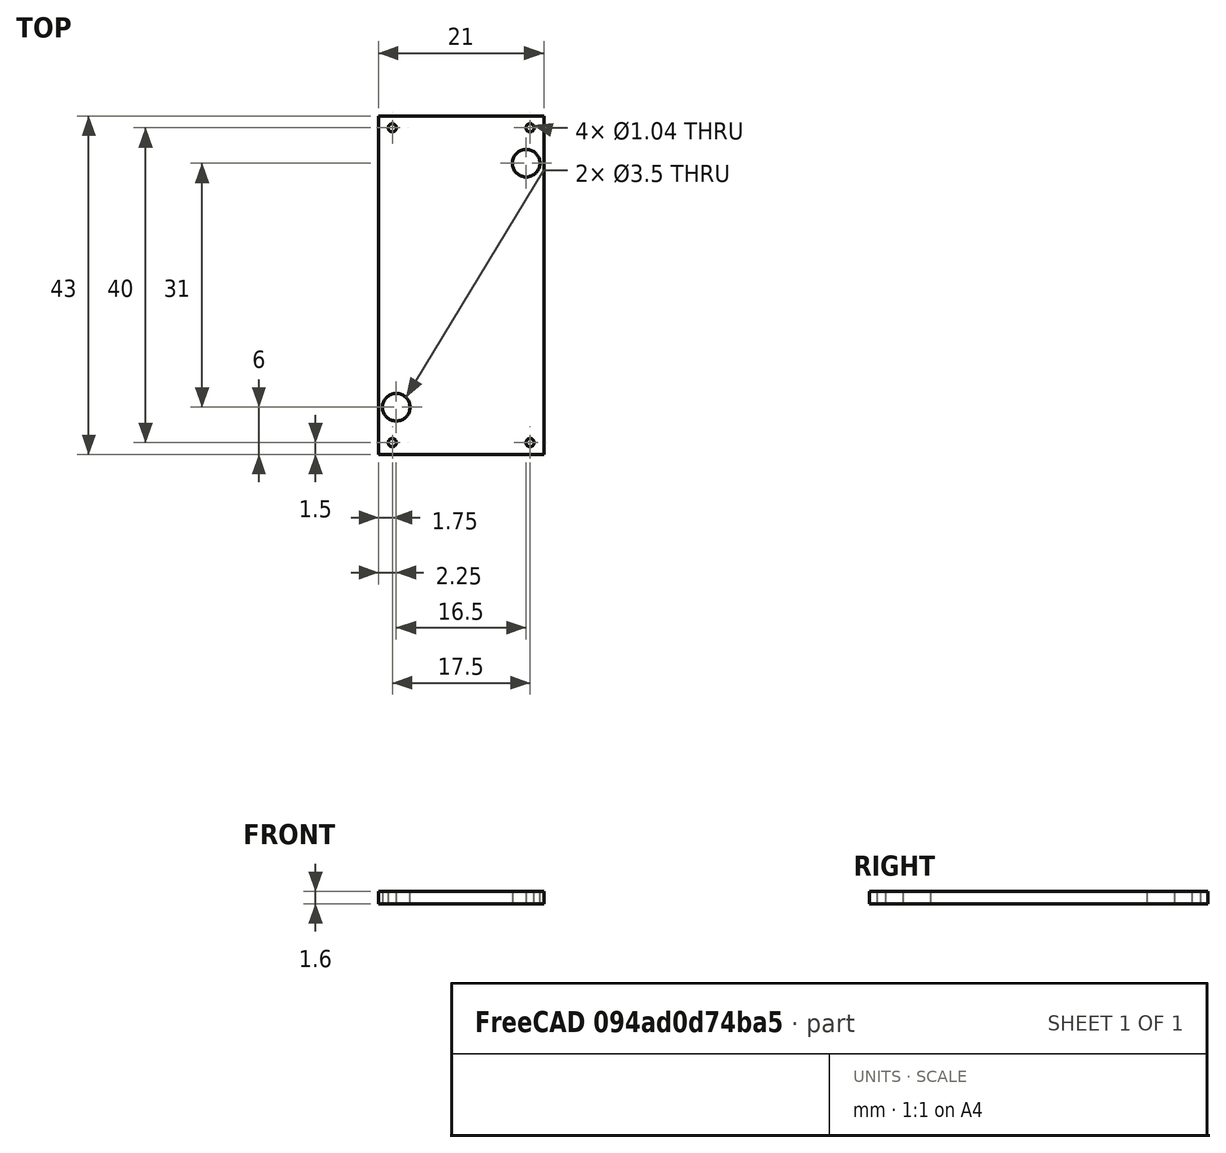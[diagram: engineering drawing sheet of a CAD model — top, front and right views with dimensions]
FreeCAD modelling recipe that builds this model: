
FCSTD DOCUMENT  (FreeCAD 0.20R27422 (Git))
Label: LM2596_Board
License: All rights reserved
LicenseURL: http://en.wikipedia.org/wiki/All_rights_reserved
objects: Sketcher::SketchObject×2, PartDesign::Pad×1, PartDesign::Body×1
note: 5 computed .brp shape members not serialized (recipe doc carries the construction recipe); baked Part::Feature solids carry a one-line shape summary decoded from their .brp

FEATURE [Sketcher::SketchObject] Sketch
  FullyConstrained = true
  MapMode = 5
  Support = -> [XY_Plane]
  sketch-geometry (11):
    g0: LineSegment StartX=-10.5 StartY=21.5 StartZ=0 EndX=10.5 EndY=21.5 EndZ=0
    g1: LineSegment StartX=10.5 StartY=21.5 StartZ=0 EndX=10.5 EndY=-21.5 EndZ=0
    g2: LineSegment StartX=10.5 StartY=-21.5 StartZ=0 EndX=-10.5 EndY=-21.5 EndZ=0
    g3: LineSegment StartX=-10.5 StartY=-21.5 StartZ=0 EndX=-10.5 EndY=21.5 EndZ=0
    g4: Circle CenterX=-8.75 CenterY=20 CenterZ=0 NormalX=0 NormalY=0 NormalZ=1 AngleXU=0 Radius=0.52
    g5: Circle CenterX=8.75 CenterY=20 CenterZ=0 NormalX=0 NormalY=0 NormalZ=1 AngleXU=0 Radius=0.52
    g6: LineSegment StartX=-8.75 StartY=20 StartZ=0 EndX=8.75 EndY=20 EndZ=0
    g7: Circle CenterX=-8.75 CenterY=-20 CenterZ=0 NormalX=0 NormalY=0 NormalZ=1 AngleXU=0 Radius=0.52
    g8: Circle CenterX=8.75 CenterY=-20 CenterZ=0 NormalX=0 NormalY=0 NormalZ=1 AngleXU=0 Radius=0.52
    g9: Circle CenterX=-8.25 CenterY=-15.5 CenterZ=0 NormalX=0 NormalY=0 NormalZ=1 AngleXU=0 Radius=1.75
    g10: Circle CenterX=8.25 CenterY=15.5 CenterZ=0 NormalX=0 NormalY=0 NormalZ=1 AngleXU=0 Radius=1.75
  constraints (27):
    c: Coincident(g0,g1)
    c: Coincident(g1,g2)
    c: Coincident(g2,g3)
    c: Coincident(g3,g0)
    c: Horizontal(g0)
    c: Horizontal(g2)
    c: Vertical(g1)
    c: Vertical(g3)
    c: Symmetric(g0,g1,g-1)
    c: DistanceX(g0,g0) = 21
    c: DistanceY(g3,g3) = 43
    c: Coincident(g6,g4)
    c: Coincident(g6,g5)
    c: DistanceX(g6,g6) = 17.5
    c: Symmetric(g5,g4,g-2)
    c: Symmetric(g5,g7,g-1)
    c: Symmetric(g8,g4,g-1)
    c: DistanceY(g7,g4) = 40
    c: Equal(g8,g7)
    c: Equal(g7,g5)
    c: Equal(g5,g4)
    c: Diameter(g8) = 1.04
    c: Diameter(g9) = 3.5
    c: DistanceY(g8,g9) = 4.5
    c: Equal(g10,g9)
    c: Symmetric(g10,g9,g-1)
    c: DistanceX(g7,g9) = 0.5
FEATURE [PartDesign::Pad] Pad
  Direction = (0,0,1)
  Length = 1.6
  Length2 = 10
  Profile = -> Sketch
  ReferenceAxis = -> Sketch [N_Axis]
  Type = 0
FEATURE [Sketcher::SketchObject] Sketch001
  ExternalGeometry = -> [Pad]
  FullyConstrained = true
  MapMode = 5
  Placement = pos=(0,0,1.6) rot=(0,0,1;0rad)
  Support = -> [Pad]
  sketch-geometry (20):
    g0: LineSegment StartX=7.2 StartY=21.5 StartZ=0 EndX=10.5 EndY=21.5 EndZ=0
    g1: LineSegment StartX=10.5 StartY=21.5 StartZ=0 EndX=10.5 EndY=18.2 EndZ=0
    g2: LineSegment StartX=10.5 StartY=18.2 StartZ=0 EndX=7.2 EndY=18.2 EndZ=0
    g3: LineSegment StartX=7.2 StartY=18.2 StartZ=0 EndX=7.2 EndY=21.5 EndZ=0
    g4: LineSegment StartX=-10.5 StartY=21.5 StartZ=0 EndX=-7.2 EndY=21.5 EndZ=0
    g5: LineSegment StartX=-7.2 StartY=21.5 StartZ=0 EndX=-7.2 EndY=18.2 EndZ=0
    g6: LineSegment StartX=-7.2 StartY=18.2 StartZ=0 EndX=-10.5 EndY=18.2 EndZ=0
    g7: LineSegment StartX=-10.5 StartY=18.2 StartZ=0 EndX=-10.5 EndY=21.5 EndZ=0
    g8: LineSegment StartX=10.5 StartY=-21.5 StartZ=0 EndX=7.2 EndY=-21.5 EndZ=0
    g9: LineSegment StartX=7.2 StartY=-21.5 StartZ=0 EndX=7.2 EndY=-18.2 EndZ=0
    g10: LineSegment StartX=7.2 StartY=-18.2 StartZ=0 EndX=10.5 EndY=-18.2 EndZ=0
    g11: LineSegment StartX=10.5 StartY=-18.2 StartZ=0 EndX=10.5 EndY=-21.5 EndZ=0
    g12: LineSegment StartX=-10.5 StartY=-21.5 StartZ=0 EndX=-7.2 EndY=-21.5 EndZ=0
    g13: LineSegment StartX=-7.2 StartY=-21.5 StartZ=0 EndX=-7.2 EndY=-18.2 EndZ=0
    g14: LineSegment StartX=-7.2 StartY=-18.2 StartZ=0 EndX=-10.5 EndY=-18.2 EndZ=0
    g15: LineSegment StartX=-10.5 StartY=-18.2 StartZ=0 EndX=-10.5 EndY=-21.5 EndZ=0
    g16: LineSegment StartX=-10.5 StartY=17.7 StartZ=0 EndX=-10.5 EndY=-17.7 EndZ=0
    g17: LineSegment StartX=10.5 StartY=17.7 StartZ=0 EndX=10.5 EndY=-17.7 EndZ=0
    g18: LineSegment StartX=-6.7 StartY=21.5 StartZ=0 EndX=6.7 EndY=21.5 EndZ=0
    g19: LineSegment StartX=-6.7 StartY=-21.5 StartZ=0 EndX=6.7 EndY=-21.5 EndZ=0
  constraints (52):
    c: Coincident(g0,g1)
    c: Coincident(g1,g2)
    c: Coincident(g2,g3)
    c: Coincident(g3,g0)
    c: Horizontal(g2)
    c: Vertical(g3)
    c: DistanceX(g0,g0) = 3.3
    c: Equal(g0,g3)
    c: Tangent(g0,g-7)
    c: Tangent(g-8,g1)
    c: Coincident(g4,g5)
    c: Coincident(g5,g6)
    c: Coincident(g6,g7)
    c: Coincident(g7,g4)
    c: Horizontal(g4)
    c: Horizontal(g6)
    c: Vertical(g5)
    c: Vertical(g7)
    c: Coincident(g4,g-7)
    c: Symmetric(g5,g2,g-2)
    c: Coincident(g8,g9)
    c: Coincident(g9,g10)
    c: Coincident(g10,g11)
    c: Coincident(g11,g8)
    c: Horizontal(g8)
    c: Horizontal(g10)
    c: Vertical(g9)
    c: Vertical(g11)
    c: Coincident(g8,g-8)
    c: Symmetric(g9,g2,g-1)
    c: Coincident(g12,g13)
    c: Coincident(g13,g14)
    c: Coincident(g14,g15)
    c: Coincident(g15,g12)
    c: Horizontal(g12)
    c: Horizontal(g14)
    c: Vertical(g13)
    c: Vertical(g15)
    c: Coincident(g12,g-10)
    c: Symmetric(g13,g9,g-2)
    c: PointOnObject(g16,g-10)
    c: PointOnObject(g17,g-8)
    c: PointOnObject(g18,g-7)
    c: PointOnObject(g19,g-9)
    c: Symmetric(g18,g18,g-2)
    c: DistanceX(g4,g18) = 0.5
    c: DistanceY(g16,g6) = 0.5
    c: Symmetric(g16,g16,g-1)
    c: Symmetric(g19,g19,g-2)
    c: Equal(g18,g19)
    c: Equal(g17,g16)
    c: Symmetric(g17,g17,g-1)
FEATURE [PartDesign::Body] Body
  Group = -> [Sketch,Pad,Sketch001]
  Origin = -> Origin
  Tip = -> Pad
